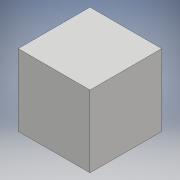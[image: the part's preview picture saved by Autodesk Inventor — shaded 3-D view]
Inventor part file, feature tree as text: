
AUTODESK INVENTOR PART (.ipt)
format: ipt  version: 2017 (Build 210142000, 142)  size: 471,552 bytes
history: native  units: mm
features: extrude x2, sketch x2
ambient origin geometry x8: Origin, YZ Plane, XZ Plane, XY Plane, X Axis, Y Axis, Z Axis, Center Point
bodies: Solid1 (feature_tree)
feature tree (4):
  extrude  "Extrusion1"  Depth=56.65mm TaperAngle=0.0deg
  extrude  "Extrusion2"  [1 undecoded]
  sketch  "Sketch1"  dims[d1=56.65mm d2=56.65mm d3=0.0mm]
  sketch  "Sketch2"  dims[d4=2.0mm d5=0.0mm]
note: 1 required parameter value undecoded (feature->parameter linkage not recoverable at this tier; creation-order binding heuristic only, values carry confidence <= 0.55)
